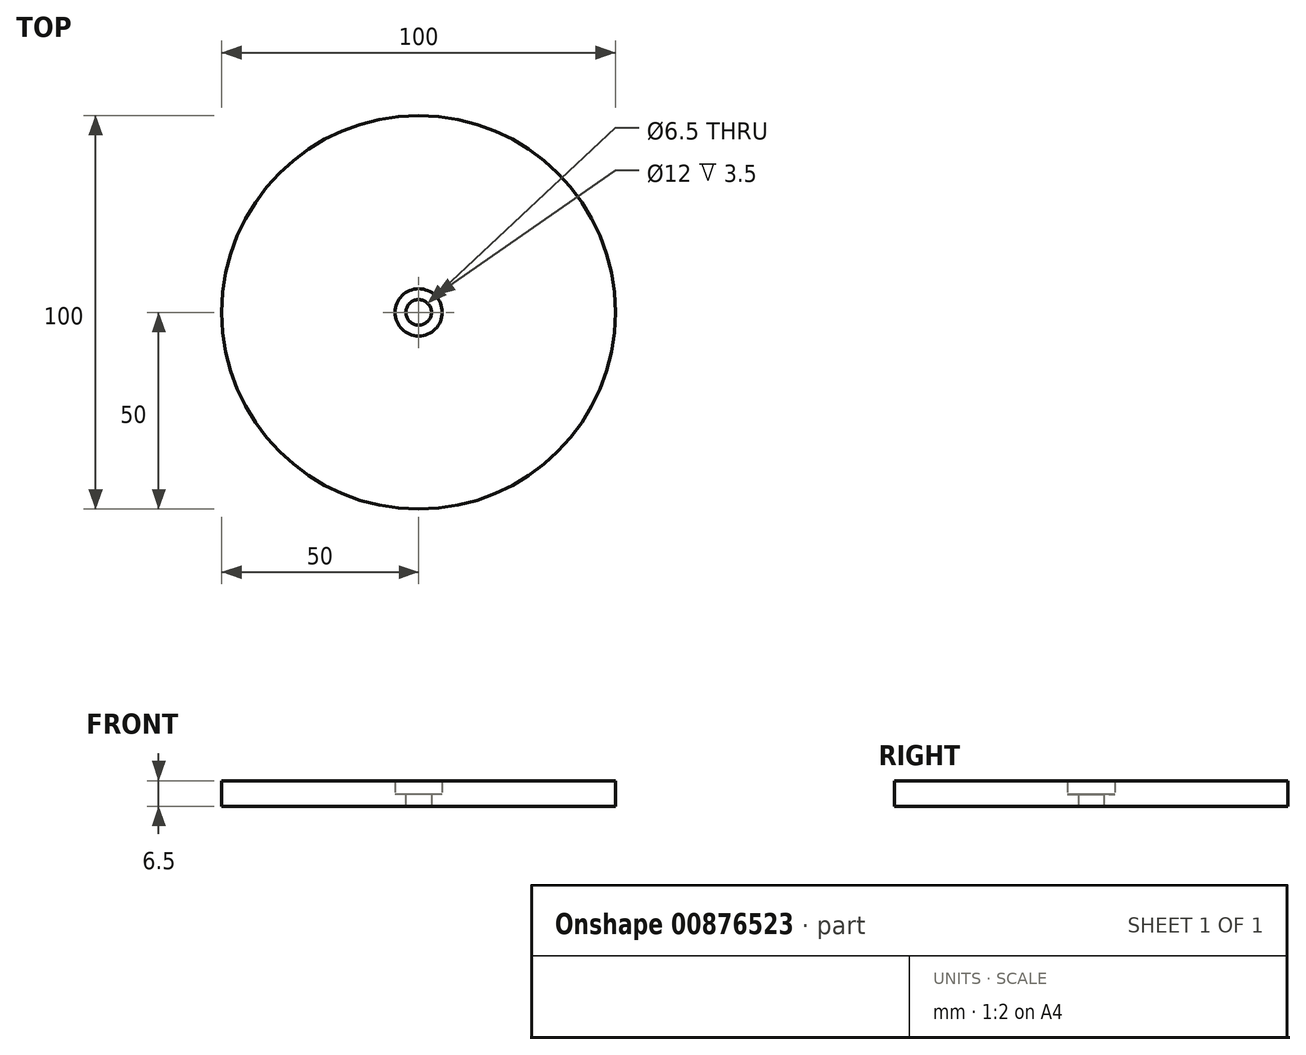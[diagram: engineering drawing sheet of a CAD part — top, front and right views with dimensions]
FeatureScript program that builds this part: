
annotation { "Feature Type Name" : "Feature", "Feature Type Description" : "" }
export const myFeature = defineFeature(function(context is Context, id is Id, definition is map)
    precondition{}
    {
        {
            var Q0;
            Q0=qCreatedBy(makeId("Top.planeOp"),FACE);
            var sketch = newSketch(context, id + "F0", { "sketchPlane" : qUnion([Q0])});
            skCircle(sketch, "E0", {"center": v(0, 0) * mm, "radius": 50 * mm});
            skCircle(sketch, "E1", {"center": v(0, 0) * mm, "radius": 45 * mm});
            skCircle(sketch, "E2", {"center": v(0, 0) * mm, "radius": 3.25 * mm});
            skSolve(sketch);
        }
        {
            var Q0;
            Q0=qSketchRegion(id+"F0",true);
            var Q1;
            Q1=makeQuery(id+"F0.imprint","IMPRINT",FACE,{"disambiguationData":[TD([[makeQuery(id+"F0.imprint","IMPRINT",EDGE,{"derivedFrom":sQuery(id+"F0.wireOp",EDGE,"E1")}),1.0]])]});
            extrude(context, id + "F1", {"entities" : qUnion([Q0, Q1]), "depth" : 3 * mm, "offsetDistance" : 25 * mm});
        }
        {
            var Q0;
            Q0=makeQuery(id+"F1.opExtrude","CAP_FACE",FACE,{"disambiguationData":[OSD([sQuery(id+"F0.wireOp",EDGE,"E0"),sQuery(id+"F0.wireOp",EDGE,"E2")])],"isStart":false});
            var sketch = newSketch(context, id + "F2", { "sketchPlane" : qUnion([Q0])});
            skCircle(sketch, "E3", {"center": v(0, 0) * mm, "radius": 50 * mm});
            skCircle(sketch, "E4", {"center": v(0, 0) * mm, "radius": 6 * mm});
            skSolve(sketch);
        }
        {
            var Q0;
            Q0 = qSketchRegion(id + "F2", true);
            extrude(context, id + "F3", {"entities" : qUnion([Q0]), "operationType" : NewBodyOperationType.ADD, "depth" : 3.5 * mm, "offsetDistance" : 25 * mm});
        }
    });
